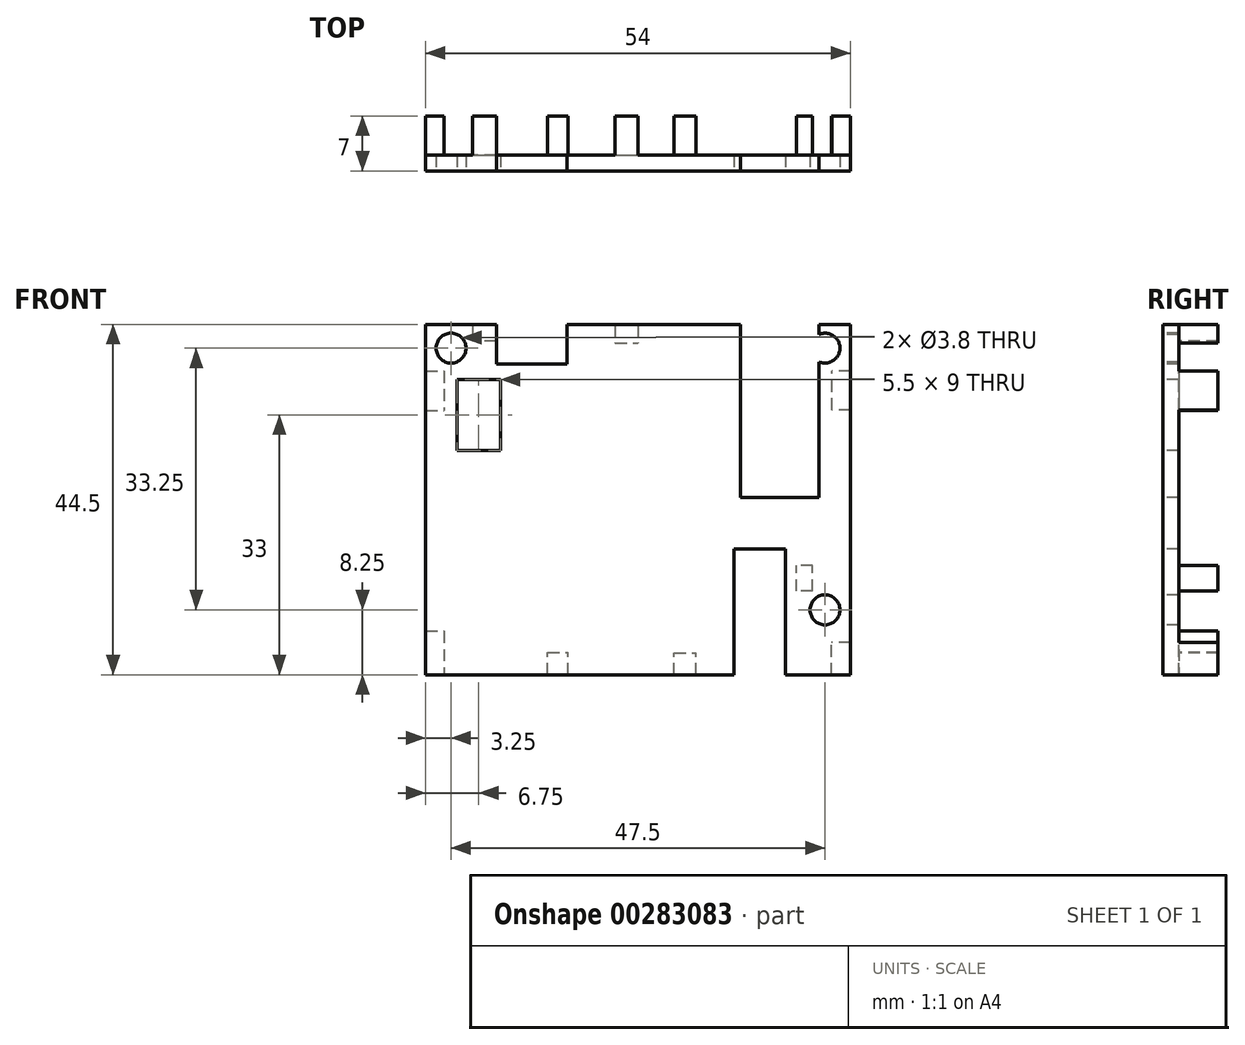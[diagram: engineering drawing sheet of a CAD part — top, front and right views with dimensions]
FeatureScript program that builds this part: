
annotation { "Feature Type Name" : "Feature", "Feature Type Description" : "" }
export const myFeature = defineFeature(function(context is Context, id is Id, definition is map)
    precondition{}
    {
        {
            var Q0;
            Q0=qCreatedBy(makeId("Front.planeOp"),FACE);
            var sketch = newSketch(context, id + "F0", { "sketchPlane" : qUnion([Q0])});
            skLineSegment(sketch, "E0.bottom", {"start": v(0, 0) * mm, "end": v(9, 0) * mm});
            skLineSegment(sketch, "E0.top", {"start": v(0, -44.5) * mm, "end": v(39.2, -44.5) * mm});
            skLineSegment(sketch, "E0.left", {"start": v(0, 0) * mm, "end": v(0, -44.5) * mm});
            skLineSegment(sketch, "E0.right", {"start": v(54, 0) * mm, "end": v(54, -44.5) * mm});
            skLineSegment(sketch, "E1.top", {"start": v(9, -5) * mm, "end": v(18, -5) * mm});
            skLineSegment(sketch, "E1.left", {"start": v(9, 0) * mm, "end": v(9, -5) * mm});
            skLineSegment(sketch, "E1.right", {"start": v(18, 0) * mm, "end": v(18, -5) * mm});
            skLineSegment(sketch, "E2.top", {"start": v(40, -22) * mm, "end": v(50, -22) * mm});
            skLineSegment(sketch, "E2.left", {"start": v(40, 0) * mm, "end": v(40, -22) * mm});
            skLineSegment(sketch, "E2.right", {"start": v(50, 0) * mm, "end": v(50, -1.25) * mm});
            skLineSegment(sketch, "E3.bottom", {"start": v(39.2, -28.5) * mm, "end": v(45.7, -28.5) * mm});
            skLineSegment(sketch, "E3.left", {"start": v(39.2, -28.5) * mm, "end": v(39.2, -44.5) * mm});
            skLineSegment(sketch, "E3.right", {"start": v(45.7, -28.5) * mm, "end": v(45.7, -44.5) * mm});
            skLineSegment(sketch, "E4.bottom", {"start": v(4, -7) * mm, "end": v(9.5, -7) * mm});
            skLineSegment(sketch, "E4.top", {"start": v(4, -16) * mm, "end": v(9.5, -16) * mm});
            skLineSegment(sketch, "E4.left", {"start": v(4, -7) * mm, "end": v(4, -16) * mm});
            skLineSegment(sketch, "E4.right", {"start": v(9.5, -7) * mm, "end": v(9.5, -16) * mm});
            skCircle(sketch, "E5", {"center": v(3.25, -3) * mm, "radius": 1.9 * mm});
            skArc(sketch, "E6", {"start": v(50, -4.75) * mm, "mid": v(52.65, -3) * mm, "end": v(50, -1.25) * mm});
            skCircle(sketch, "E7", {"center": v(50.75, -36.25) * mm, "radius": 1.9 * mm});
            skLineSegment(sketch, "E8.trimOffspring", {"start": v(50, -4.75) * mm, "end": v(50, -22) * mm});
            skLineSegment(sketch, "E9.trimOffspring", {"start": v(18, 0) * mm, "end": v(40, 0) * mm});
            skLineSegment(sketch, "E10.trimOffspring", {"start": v(45.7, -44.5) * mm, "end": v(54, -44.5) * mm});
            skLineSegment(sketch, "E11.trimOffspring", {"start": v(50, 0) * mm, "end": v(54, 0) * mm});
            skSolve(sketch);
        }
        {
            var Q0;
            Q0 = qSketchRegion(id + "F0", true);
            extrude(context, id + "F1", {"entities" : qUnion([Q0]), "oppositeDirection" : true, "depth" : 2 * mm});
        }
        {
            var Q0;
            Q0=makeQuery(id+"F1.opExtrude","CAP_FACE",FACE,{"disambiguationData":[OSD([sQuery(id+"F0.wireOp",EDGE,"E0.bottom"),sQuery(id+"F0.wireOp",EDGE,"E0.top"),sQuery(id+"F0.wireOp",EDGE,"E0.left"),sQuery(id+"F0.wireOp",EDGE,"E0.right"),sQuery(id+"F0.wireOp",EDGE,"E1.top"),sQuery(id+"F0.wireOp",EDGE,"E1.left"),sQuery(id+"F0.wireOp",EDGE,"E1.right"),sQuery(id+"F0.wireOp",EDGE,"E2.top"),sQuery(id+"F0.wireOp",EDGE,"E2.left"),sQuery(id+"F0.wireOp",EDGE,"E2.right"),sQuery(id+"F0.wireOp",EDGE,"E3.bottom"),sQuery(id+"F0.wireOp",EDGE,"E3.left"),sQuery(id+"F0.wireOp",EDGE,"E3.right"),sQuery(id+"F0.wireOp",EDGE,"E4.bottom"),sQuery(id+"F0.wireOp",EDGE,"E4.top"),sQuery(id+"F0.wireOp",EDGE,"E4.left"),sQuery(id+"F0.wireOp",EDGE,"E4.right"),sQuery(id+"F0.wireOp",EDGE,"E5"),sQuery(id+"F0.wireOp",EDGE,"E6"),sQuery(id+"F0.wireOp",EDGE,"E7"),sQuery(id+"F0.wireOp",EDGE,"E8.trimOffspring"),sQuery(id+"F0.wireOp",EDGE,"E9.trimOffspring"),sQuery(id+"F0.wireOp",EDGE,"E10.trimOffspring"),sQuery(id+"F0.wireOp",EDGE,"E11.trimOffspring")])],"isStart":false});
            var sketch = newSketch(context, id + "F2", { "sketchPlane" : qUnion([Q0])});
            skLineSegment(sketch, "E12.bottom", {"start": v(0, -5.91) * mm, "end": v(-2.33, -5.91) * mm});
            skLineSegment(sketch, "E12.top", {"start": v(0, -10.96) * mm, "end": v(-2.33, -10.96) * mm});
            skLineSegment(sketch, "E12.left", {"start": v(0, -5.91) * mm, "end": v(0, -10.96) * mm});
            skLineSegment(sketch, "E12.right", {"start": v(-2.33, -5.91) * mm, "end": v(-2.33, -10.96) * mm});
            skLineSegment(sketch, "E13.bottom", {"start": v(0, -38.95) * mm, "end": v(-2.33, -38.95) * mm});
            skLineSegment(sketch, "E13.top", {"start": v(0, -44.5) * mm, "end": v(-2.33, -44.5) * mm});
            skLineSegment(sketch, "E13.left", {"start": v(0, -38.95) * mm, "end": v(0, -44.5) * mm});
            skLineSegment(sketch, "E13.right", {"start": v(-2.33, -38.95) * mm, "end": v(-2.33, -44.5) * mm});
            skLineSegment(sketch, "E14.bottom", {"start": v(-15.5, -44.5) * mm, "end": v(-18.08, -44.5) * mm});
            skLineSegment(sketch, "E14.top", {"start": v(-15.5, -41.63) * mm, "end": v(-18.08, -41.63) * mm});
            skLineSegment(sketch, "E14.left", {"start": v(-15.5, -44.5) * mm, "end": v(-15.5, -41.63) * mm});
            skLineSegment(sketch, "E14.right", {"start": v(-18.08, -44.5) * mm, "end": v(-18.08, -41.63) * mm});
            skLineSegment(sketch, "E15.bottom", {"start": v(-31.57, -44.5) * mm, "end": v(-34.35, -44.5) * mm});
            skLineSegment(sketch, "E15.top", {"start": v(-31.57, -41.73) * mm, "end": v(-34.35, -41.73) * mm});
            skLineSegment(sketch, "E15.left", {"start": v(-31.57, -44.5) * mm, "end": v(-31.57, -41.73) * mm});
            skLineSegment(sketch, "E15.right", {"start": v(-34.35, -44.5) * mm, "end": v(-34.35, -41.73) * mm});
            skLineSegment(sketch, "E16.bottom", {"start": v(-54, -44.5) * mm, "end": v(-51.54, -44.5) * mm});
            skLineSegment(sketch, "E16.top", {"start": v(-54, -40.4) * mm, "end": v(-51.54, -40.4) * mm});
            skLineSegment(sketch, "E16.left", {"start": v(-54, -44.5) * mm, "end": v(-54, -40.4) * mm});
            skLineSegment(sketch, "E16.right", {"start": v(-51.54, -44.5) * mm, "end": v(-51.54, -40.4) * mm});
            skLineSegment(sketch, "E17.bottom", {"start": v(-54, -10.85) * mm, "end": v(-51.64, -10.85) * mm});
            skLineSegment(sketch, "E17.top", {"start": v(-54, -5.91) * mm, "end": v(-51.64, -5.91) * mm});
            skLineSegment(sketch, "E17.left", {"start": v(-54, -10.85) * mm, "end": v(-54, -5.91) * mm});
            skLineSegment(sketch, "E17.right", {"start": v(-51.64, -10.85) * mm, "end": v(-51.64, -5.91) * mm});
            skLineSegment(sketch, "E18.bottom", {"start": v(-24.07, 0) * mm, "end": v(-26.99, 0) * mm});
            skLineSegment(sketch, "E18.top", {"start": v(-24.07, -2.37) * mm, "end": v(-26.99, -2.37) * mm});
            skLineSegment(sketch, "E18.left", {"start": v(-24.07, 0) * mm, "end": v(-24.07, -2.37) * mm});
            skLineSegment(sketch, "E18.right", {"start": v(-26.99, 0) * mm, "end": v(-26.99, -2.37) * mm});
            skLineSegment(sketch, "E19.bottom", {"start": v(-9, 0) * mm, "end": v(-5.98, 0) * mm});
            skLineSegment(sketch, "E19.top", {"start": v(-9, -2.13) * mm, "end": v(-5.98, -2.13) * mm});
            skLineSegment(sketch, "E19.left", {"start": v(-9, 0) * mm, "end": v(-9, -2.13) * mm});
            skLineSegment(sketch, "E19.right", {"start": v(-5.98, 0) * mm, "end": v(-5.98, -2.13) * mm});
            skLineSegment(sketch, "E20.bottom", {"start": v(-49.18, -33.88) * mm, "end": v(-47.13, -33.88) * mm});
            skLineSegment(sketch, "E20.top", {"start": v(-49.18, -30.64) * mm, "end": v(-47.13, -30.64) * mm});
            skLineSegment(sketch, "E20.left", {"start": v(-49.18, -33.88) * mm, "end": v(-49.18, -30.64) * mm});
            skLineSegment(sketch, "E20.right", {"start": v(-47.13, -33.88) * mm, "end": v(-47.13, -30.64) * mm});
            skSolve(sketch);
        }
        {
            var Q0;
            Q0 = qSketchRegion(id + "F2", true);
            extrude(context, id + "F3", {"entities" : qUnion([Q0]), "operationType" : NewBodyOperationType.ADD, "depth" : 5 * mm});
        }
    });
